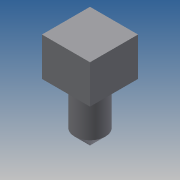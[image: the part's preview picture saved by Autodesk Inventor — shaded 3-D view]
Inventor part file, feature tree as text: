
AUTODESK INVENTOR PART (.ipt)
format: ipt  version: 2013 (Build 170138000, 138)  size: 85,504 bytes
history: native  units: mm
features: revolve x1, extrude x1, sketch x1
ambient origin geometry x8: Origin, YZ Plane, XZ Plane, XY Plane, X Axis, Y Axis, Z Axis, Center Point
bodies: Solid1 (feature_tree)
feature tree (3):
  revolve  "Revolution1"  [1 undecoded]
  extrude  "Extrusion1"  TaperAngle=135.0deg  [1 undecoded]
  sketch  "Sketch2"  dims[d0=50.0mm d1=8.0mm d2=135.0deg d3=90.0deg d4=25.0mm d6=25.0mm d7=20.0mm d8=0.0mm]
note: 2 required parameter values undecoded (feature->parameter linkage not recoverable at this tier; creation-order binding heuristic only, values carry confidence <= 0.55)